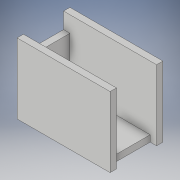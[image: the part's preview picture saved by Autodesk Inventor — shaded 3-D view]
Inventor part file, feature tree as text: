
AUTODESK INVENTOR PART (.ipt)
format: ipt  version: 2019 (Build 230136000, 136)  size: 120,832 bytes
history: native  units: mm
features: extrude x3, sketch x3, projected_geometry x2
ambient origin geometry x8: Origin, YZ Plane, XZ Plane, XY Plane, X Axis, Y Axis, Z Axis, Center Point
bodies: Solid1 (feature_tree)
feature tree (8):
  extrude  "Extrusion1"  Depth=20.0mm
  extrude  "Extrusion2"  Depth=3.18mm
  extrude  "Extrusion3"  Depth=3.18mm
  sketch  "Sketch2"  dims[d25=40.0mm d26=20.0mm]
  sketch  "Sketch5"  dims[d27=3.18mm d28=0.0mm d34=3.18mm]
  projected_geometry  "Projected Loop2"
  sketch  "Sketch6"  dims[d35=3.18mm d36=3.18mm d37=35.0mm d38=0.0mm d39=3.18mm d40=20.0mm d41=27.0mm d42=0.0mm]
  projected_geometry  "Projected Loop3"
